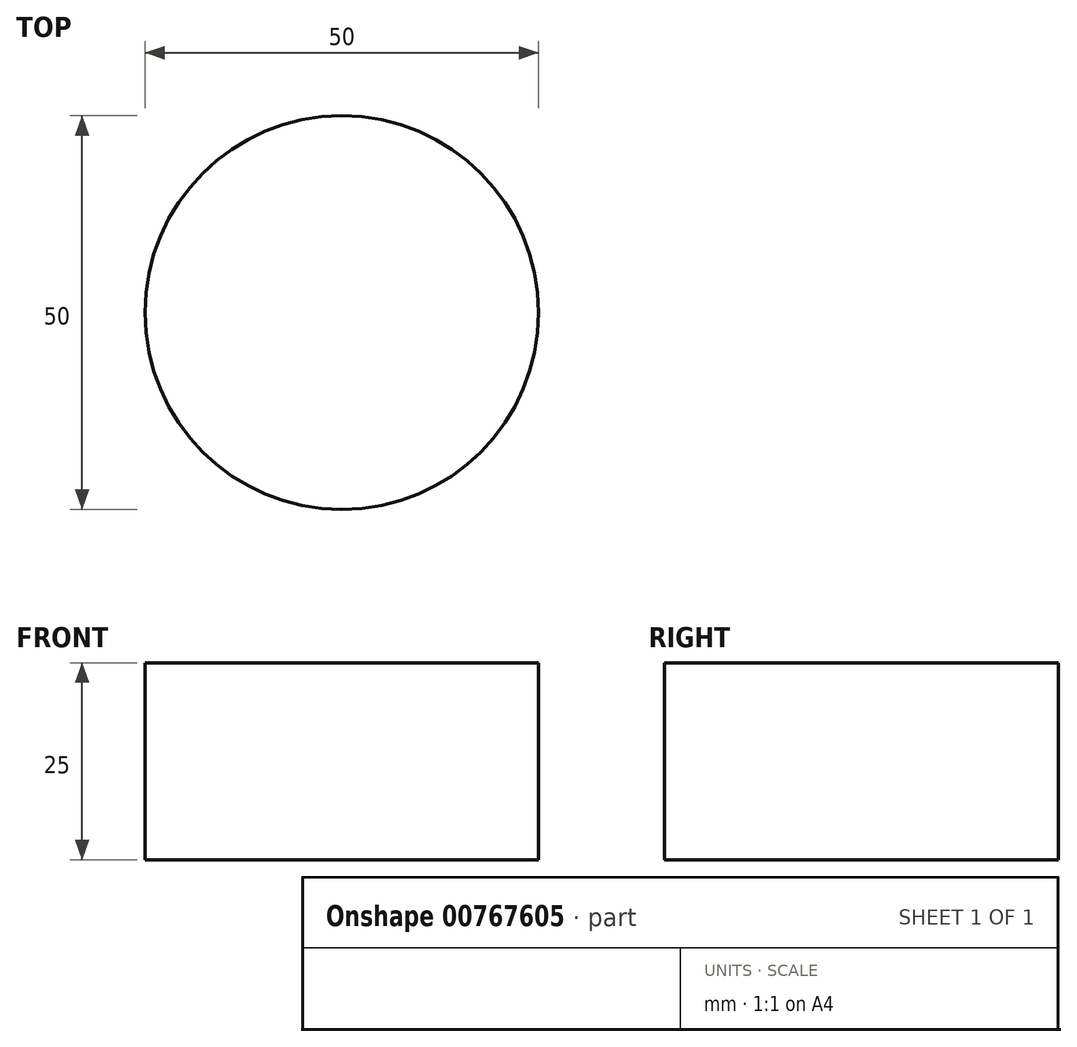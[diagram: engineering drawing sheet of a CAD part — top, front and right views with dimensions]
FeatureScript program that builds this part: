
annotation { "Feature Type Name" : "Feature", "Feature Type Description" : "" }
export const myFeature = defineFeature(function(context is Context, id is Id, definition is map)
    precondition{}
    {
        {
            var Q0;
            Q0=qCreatedBy(makeId("Top.planeOp"),FACE);
            var sketch = newSketch(context, id + "F0", { "sketchPlane" : qUnion([Q0])});
            skCircle(sketch, "E0", {"center": v(-23.35, 21.3) * mm, "radius": 25 * mm});
            skSolve(sketch);
        }
        {
            var Q0;
            Q0=makeQuery(id+"F0.imprint","IMPRINT",FACE,{"disambiguationData":[TD([[makeQuery(id+"F0.imprint","IMPRINT",EDGE,{"derivedFrom":sQuery(id+"F0.wireOp",EDGE,"E0")}),1.0]])]});
            extrude(context, id + "F1", {"entities" : qUnion([Q0]), "depth" : 25 * mm, "offsetDistance" : 25 * mm});
        }
    });
